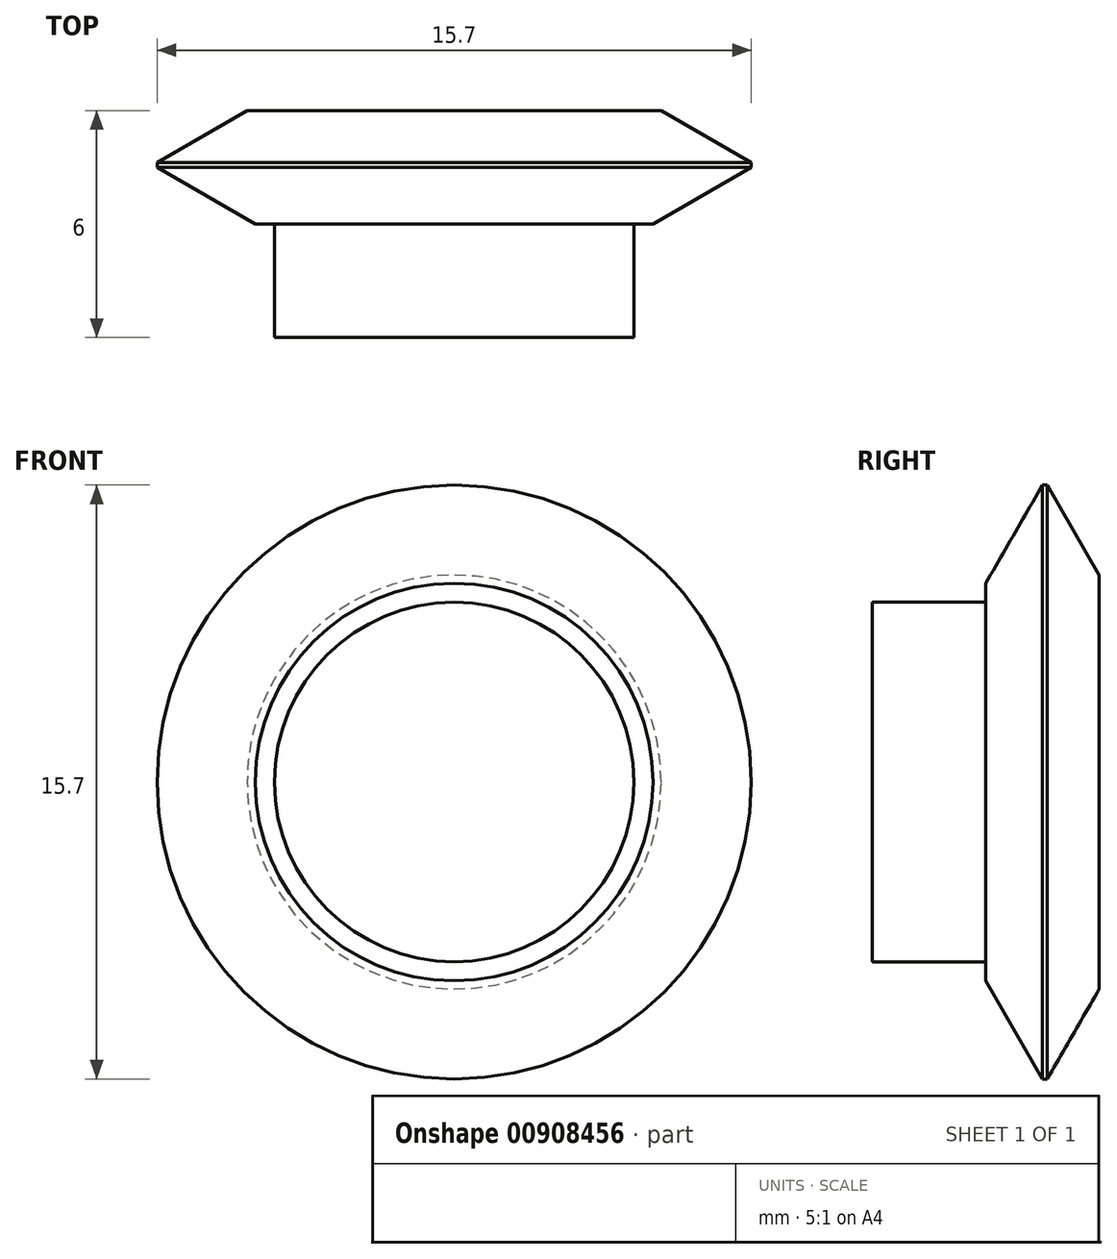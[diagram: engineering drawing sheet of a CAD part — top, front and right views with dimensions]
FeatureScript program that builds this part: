
annotation { "Feature Type Name" : "Feature", "Feature Type Description" : "" }
export const myFeature = defineFeature(function(context is Context, id is Id, definition is map)
    precondition{}
    {
        {
            var Q0;
            Q0=qCreatedBy(makeId("Front.planeOp"),FACE);
            var sketch = newSketch(context, id + "F0", { "sketchPlane" : qUnion([Q0])});
            skCircle(sketch, "E0", {"center": v(0, 0) * mm, "radius": 7.85 * mm});
            skSolve(sketch);
        }
        {
            var Q0;
            Q0 = qSketchRegion(id + "F0", true);
            extrude(context, id + "F1", {"entities" : qUnion([Q0]), "depth" : 3 * mm, "offsetDistance" : 25 * mm});
        }
        {
            var Q0;
            Q0=makeQuery(id+"F1.opExtrude","CAP_FACE",FACE,{"disambiguationData":[OSD([sQuery(id+"F0.wireOp",EDGE,"E0")])],"isStart":false});
            var sketch = newSketch(context, id + "F2", { "sketchPlane" : qUnion([Q0])});
            skCircle(sketch, "E1", {"center": v(0, 0) * mm, "radius": 4.75 * mm});
            skSolve(sketch);
        }
        {
            var Q0;
            Q0 = qSketchRegion(id + "F2", true);
            extrude(context, id + "F3", {"entities" : qUnion([Q0]), "operationType" : NewBodyOperationType.ADD, "depth" : 3 * mm, "offsetDistance" : 25 * mm});
        }
        {
            var Q0;
            Q0=qCreatedBy(makeId("Right.planeOp"),FACE);
            var sketch = newSketch(context, id + "F4", { "sketchPlane" : qUnion([Q0])});
            skLineSegment(sketch, "E2", {"start": v(-1.44, 7.96) * mm, "end": v(-3.14, 5.01) * mm});
            skLineSegment(sketch, "E3", {"start": v(-1.44, 7.96) * mm, "end": v(0.27, 5.01) * mm});
            skLineSegment(sketch, "E4", {"start": v(-3.14, 5.01) * mm, "end": v(-3.54, 9.2) * mm});
            skLineSegment(sketch, "E5", {"start": v(-3.54, 9.2) * mm, "end": v(1.44, 8.55) * mm});
            skLineSegment(sketch, "E6", {"start": v(1.44, 8.55) * mm, "end": v(0.27, 5.01) * mm});
            skLineSegment(sketch, "E7", {"start": v(0, 0) * mm, "end": v(-9.6, 0) * mm});
            skSolve(sketch);
        }
        {
            var Q0;
            Q0 = qSketchRegion(id + "F4", true);
            var Q1;
            Q1=sQuery(id+"F4.wireOp",EDGE,"E7");
            revolve(context, id + "F5", {"operationType" : NewBodyOperationType.REMOVE, "surfaceOperationType" : NewSurfaceOperationType.NEW, "entities" : qUnion([Q0]), "axis" : qUnion([Q1]), "revolveType" : RevolveType.FULL, "oppositeDirection" : true});
        }
    });
